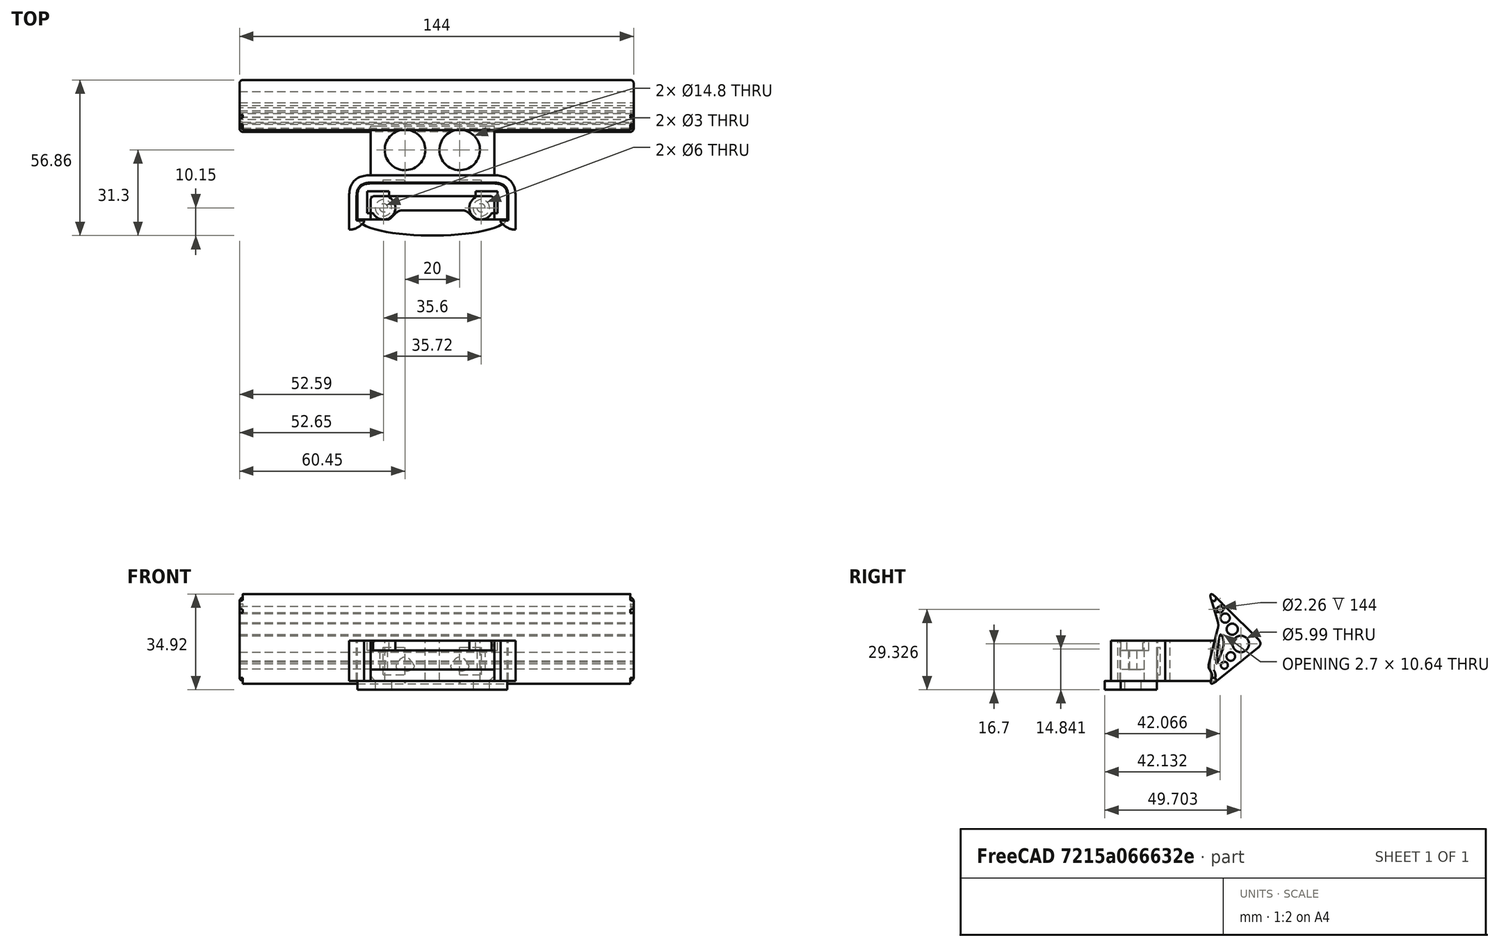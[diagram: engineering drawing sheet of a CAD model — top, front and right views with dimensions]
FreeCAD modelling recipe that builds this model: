
FCSTD DOCUMENT  (FreeCAD 0.19R0.19.2)
Label: 038
License: All rights reserved
LicenseURL: http://en.wikipedia.org/wiki/All_rights_reserved
objects: Sketcher::SketchObject×6, Part::Extrusion×6, Part::Cylinder×4, Part::Box×3, Part::Fillet×3, Part::MultiFuse×2, Part::Cut×2
note: 26 computed .brp shape members not serialized (recipe doc carries the construction recipe); baked Part::Feature solids carry a one-line shape summary decoded from their .brp

FEATURE [Sketcher::SketchObject] Sketch  label="attatchmentPiece"
  FullyConstrained = true
  sketch-geometry (20):
    g0: Circle CenterX=16.25 CenterY=0 CenterZ=0 NormalX=0 NormalY=0 NormalZ=1 AngleXU=0 Radius=1.5
    g1: LineSegment StartX=21.05 StartY=0 StartZ=0 EndX=21.05 EndY=-1 EndZ=0
    g2: LineSegment StartX=21.05 StartY=-1 StartZ=0 EndX=21.05 EndY=-4.3 EndZ=0
    g3: LineSegment StartX=-24.15 StartY=4.3 StartZ=0 EndX=21.05 EndY=4.3 EndZ=0
    g4: LineSegment StartX=21.05 StartY=0 StartZ=0 EndX=21.05 EndY=4.3 EndZ=0
    g5-g8: Circle x4 (B-spline internal-alignment scaffolding for g9; pole/knot coordinates omitted)
    g9: BSplineCurve PolesCount=4 KnotsCount=2 Degree=3 IsPeriodic=0
    g10: GeomPoint X=10.05 Y=-1 Z=0
    g11: GeomPoint X=14.55 Y=-4.3 Z=0
    g12: LineSegment StartX=10.05 StartY=-1 StartZ=0 EndX=-10.05 EndY=-1 EndZ=0
    g13: LineSegment StartX=14.55 StartY=-4.3 StartZ=0 EndX=21.05 EndY=-4.3 EndZ=0
    g14: LineSegment StartX=-24.15 StartY=4.3 StartZ=0 EndX=-24.15 EndY=-4.3 EndZ=0
    g15: LineSegment StartX=-13.15 StartY=-1 StartZ=0 EndX=-10.05 EndY=-1 EndZ=0
    g16: LineSegment StartX=-24.15 StartY=-4.3 StartZ=0 EndX=-19.35 EndY=-4.3 EndZ=0
    g17: Circle CenterX=-19.35 CenterY=0 CenterZ=0 NormalX=0 NormalY=0 NormalZ=1 AngleXU=0 Radius=1.5
    g18: LineSegment StartX=-19.35 StartY=-4.3 StartZ=0 EndX=-17.65 EndY=-4.3 EndZ=0
    g19: BSplineCurve PolesCount=4 KnotsCount=2 Degree=3 IsPeriodic=0
  constraints (41):
    c: Block(g0)
    c: Vertical(g1)
    c: Coincident(g2,g1)
    c: Vertical(g2)
    c: Block(g1)
    c: Horizontal(g3)
    c: Vertical(g4)
    c: Coincident(g4,g3)
    c: Block(g3)
    c: Block(g4)
    c: Weight(g5) = 1
    c: Equal(g5,g6)
    c: Equal(g5,g7)
    c: Equal(g5,g8)
    c: InternalAlignment(g5-g8 -> g9) x4
    c: InternalAlignment(g10,g9)
    c: InternalAlignment(g11,g9)
    c: Block(g9)
    c: Coincident(g12,g9)
    c: Horizontal(g12)
    c: Coincident(g13,g9)
    c: Coincident(g13,g2)
    c: Horizontal(g13)
    c: Distance(g3) = 45.2
    c: Coincident(g14,g3)
    c: Vertical(g14)
    c: Horizontal(g15)
    c: Distance(g15) = 3.1
    c: Block(g17)
    c: Horizontal(g16)
    c: Block(g19)
    c: Coincident(g18,g16)
    c: Coincident(g18,g19)
    c: Horizontal(g18)
    c: Block(g18)
    c: Coincident(g19,g15)
    c: Block(g16)
    c: Block(g12)
    c: Block(g14)
    c: Distance(g16) = 4.8
    c: Distance(g18) = 1.7
FEATURE [Part::Extrusion] Extrude  label="attatchmentPiece001"
  Base = -> Sketch
  Dir = (0,0,1)
  DirMode = 2
  FaceMakerClass = Part::FaceMakerBullseye
  LengthFwd = 7
  LengthRev = 0
  Solid = true
  Symmetric = false
FEATURE [Sketcher::SketchObject] Sketch001  label="attatchmentPieceSurround"
  FullyConstrained = true
  sketch-geometry (18):
    g0: LineSegment StartX=25.85 StartY=-4.3 StartZ=0 EndX=21.05 EndY=-4.3 EndZ=0
    g1: LineSegment StartX=25.85 StartY=-4.3 StartZ=0 EndX=25.85 EndY=4.3 EndZ=0
    g2: LineSegment StartX=-21.05 StartY=8.9 StartZ=0 EndX=21.05 EndY=8.9 EndZ=0
    g3: Circle CenterX=21.05 CenterY=8.9 CenterZ=0 NormalX=0 NormalY=0 NormalZ=1 AngleXU=0 Radius=1
    g4: Circle CenterX=25.85 CenterY=8.9 CenterZ=0 NormalX=0 NormalY=0 NormalZ=1 AngleXU=0 Radius=1
    g5: Circle CenterX=25.85 CenterY=4.3 CenterZ=0 NormalX=0 NormalY=0 NormalZ=1 AngleXU=0 Radius=1
    g6: BSplineCurve PolesCount=3 KnotsCount=2 Degree=2 IsPeriodic=0
    g7: GeomPoint X=21.05 Y=8.9 Z=0
    g8: GeomPoint X=25.85 Y=4.3 Z=0
    g9: ArcOfCircle CenterX=19.45 CenterY=2.7 CenterZ=0 NormalX=0 NormalY=0 NormalZ=1 AngleXU=0 Radius=1.6 StartAngle=0 EndAngle=1.5708
    g10: LineSegment StartX=21.05 StartY=2.7 StartZ=0 EndX=21.05 EndY=-4.3 EndZ=0
    g11: BSplineCurve PolesCount=3 KnotsCount=2 Degree=2 IsPeriodic=0
    g12: LineSegment StartX=-28.95 StartY=-4.3 StartZ=0 EndX=-28.95 EndY=4.3 EndZ=0
    g13: LineSegment StartX=-24.15 StartY=-4.3 StartZ=0 EndX=-28.95 EndY=-4.3 EndZ=0
    g14: LineSegment StartX=-24.15 StartY=2.7 StartZ=0 EndX=-24.15 EndY=-4.3 EndZ=0
    g15: ArcOfCircle CenterX=-22.55 CenterY=2.7 CenterZ=0 NormalX=0 NormalY=0 NormalZ=1 AngleXU=0 Radius=1.6 StartAngle=1.5708 EndAngle=3.14159
    g16: LineSegment StartX=-24.15 StartY=8.9 StartZ=0 EndX=-21.05 EndY=8.9 EndZ=0
    g17: LineSegment StartX=-22.55 StartY=4.3 StartZ=0 EndX=19.45 EndY=4.3 EndZ=0
  constraints (38):
    c: Horizontal(g0)
    c: Vertical(g1)
    c: Coincident(g1,g0)
    c: Horizontal(g2)
    c: Distance(g2) = 42.1
    c: Block(g2)
    c: Coincident(g6,g2)
    c: Weight(g3) = 1
    c: Equal(g3,g4)
    c: Equal(g3,g5)
    c: Coincident(g6,g1)
    c: InternalAlignment(g3,g6)
    c: InternalAlignment(g4,g6)
    c: InternalAlignment(g5,g6)
    c: InternalAlignment(g7,g6)
    c: InternalAlignment(g8,g6)
    c: Block(g0)
    c: Block(g6)
    c: Block(g9)
    c: Coincident(g10,g9)
    c: Coincident(g10,g0)
    c: Vertical(g10)
    c: Horizontal(g13)
    c: Coincident(g12,g13)
    c: Vertical(g12)
    c: Coincident(g11,g12)
    c: Block(g12)
    c: Block(g11)
    c: Block(g15)
    c: Coincident(g14,g15)
    c: Coincident(g14,g13)
    c: Vertical(g14)
    c: Coincident(g16,g11)
    c: Coincident(g16,g2)
    c: Horizontal(g16)
    c: Coincident(g17,g15)
    c: Coincident(g17,g9)
    c: Horizontal(g17)
FEATURE [Part::Extrusion] Extrude001  label="attatchmentPieceSurround001"
  Base = -> Sketch001
  Dir = (0,0,1)
  DirMode = 2
  FaceMakerClass = Part::FaceMakerBullseye
  LengthFwd = 14.7
  LengthRev = 0
  Placement = pos=(0,0,-4.1) rot=(0,0,1;0rad)
  Solid = true
  Symmetric = false
FEATURE [Sketcher::SketchObject] Sketch002  label="attatchmentPieceEndScrewHoleCaps"
  FullyConstrained = true
  sketch-geometry (10):
    g0: ArcOfCircle CenterX=16.25 CenterY=0 CenterZ=0 NormalX=0 NormalY=0 NormalZ=1 AngleXU=0 Radius=4.3 StartAngle=2.05456 EndAngle=5.79942
    g1: LineSegment StartX=14.25 StartY=3.80657 StartZ=0 EndX=14.25 EndY=6 EndZ=0
    g2: LineSegment StartX=20.0566 StartY=-2 StartZ=0 EndX=22.25 EndY=-2 EndZ=0
    g3: LineSegment StartX=22.25 StartY=-2 StartZ=0 EndX=22.25 EndY=6 EndZ=0
    g4: LineSegment StartX=14.25 StartY=6 StartZ=0 EndX=22.25 EndY=6 EndZ=0
    g5: LineSegment StartX=-25.35 StartY=-2 StartZ=0 EndX=-25.35 EndY=6 EndZ=0
    g6: LineSegment StartX=-25.35 StartY=-2 StartZ=0 EndX=-23.1566 EndY=-2 EndZ=0
    g7: LineSegment StartX=-17.35 StartY=6 StartZ=0 EndX=-25.35 EndY=6 EndZ=0
    g8: LineSegment StartX=-17.35 StartY=3.80657 StartZ=0 EndX=-17.35 EndY=6 EndZ=0
    g9: ArcOfCircle CenterX=-19.35 CenterY=0 CenterZ=0 NormalX=0 NormalY=0 NormalZ=1 AngleXU=0 Radius=4.3 StartAngle=3.62536 EndAngle=7.37022
  constraints (25):
    c: Block(g0)
    c: Vertical(g1)
    c: Horizontal(g2)
    c: Coincident(g3,g2)
    c: Vertical(g3)
    c: Coincident(g4,g1)
    c: Horizontal(g4)
    c: Coincident(g3,g4)
    c: Block(g4)
    c: Block(g3)
    c: Coincident(g0,g1)
    c: Coincident(g0,g2)
    c: Block(g1)
    c: Block(g9)
    c: Horizontal(g6)
    c: Vertical(g8)
    c: Coincident(g7,g8)
    c: Horizontal(g7)
    c: Coincident(g5,g6)
    c: Vertical(g5)
    c: Coincident(g5,g7)
    c: Block(g7)
    c: Block(g5)
    c: Coincident(g9,g6)
    c: Coincident(g9,g8)
FEATURE [Part::Extrusion] Extrude002  label="attatchmentPieceEndScrewHoleCaps001"
  Base = -> Sketch002
  Dir = (0,0,1)
  DirMode = 2
  FaceMakerClass = Part::FaceMakerBullseye
  LengthFwd = 3.6
  LengthRev = 0
  Placement = pos=(0,0,7) rot=(0,0,1;0rad)
  Solid = true
  Symmetric = false
FEATURE [Sketcher::SketchObject] Sketch003  label="mainBumpperPieceAttatchment"
  FullyConstrained = true
  sketch-geometry (42):
    g0: Circle CenterX=28.85 CenterY=4.3 CenterZ=0 NormalX=0 NormalY=0 NormalZ=1 AngleXU=0 Radius=1
    g1: Circle CenterX=28.85 CenterY=11.9 CenterZ=0 NormalX=0 NormalY=0 NormalZ=1 AngleXU=0 Radius=1
    g2: Circle CenterX=21.05 CenterY=11.9 CenterZ=0 NormalX=0 NormalY=0 NormalZ=1 AngleXU=0 Radius=1
    g3: BSplineCurve PolesCount=3 KnotsCount=2 Degree=2 IsPeriodic=0
    g4: GeomPoint X=28.85 Y=4.3 Z=0
    g5: GeomPoint X=21.05 Y=11.9 Z=0
    g6: LineSegment StartX=-21.05 StartY=11.9 StartZ=0 EndX=21.05 EndY=11.9 EndZ=0
    g7: LineSegment StartX=28.85 StartY=4.3 StartZ=0 EndX=28.85 EndY=-4.3 EndZ=0
    g8: Circle CenterX=21.05 CenterY=9.2 CenterZ=0 NormalX=0 NormalY=0 NormalZ=1 AngleXU=0 Radius=1
    g9: Circle CenterX=26.15 CenterY=9.2 CenterZ=0 NormalX=0 NormalY=0 NormalZ=1 AngleXU=0 Radius=1
    g10: Circle CenterX=26.15 CenterY=4.3 CenterZ=0 NormalX=0 NormalY=0 NormalZ=1 AngleXU=0 Radius=1
    g11: BSplineCurve PolesCount=3 KnotsCount=2 Degree=2 IsPeriodic=0
    g12: GeomPoint X=21.05 Y=9.2 Z=0
    g13: GeomPoint X=26.15 Y=4.3 Z=0
    g14: LineSegment StartX=-21.05 StartY=9.2 StartZ=0 EndX=21.05 EndY=9.2 EndZ=0
    g15: LineSegment StartX=26.15 StartY=-4.3 StartZ=0 EndX=26.15 EndY=4.3 EndZ=0
    g16: LineSegment StartX=26.15 StartY=-4.3 StartZ=0 EndX=26.15 EndY=-4.6 EndZ=0
    g17: LineSegment StartX=23.45 StartY=-4.6 StartZ=0 EndX=26.15 EndY=-4.6 EndZ=0
    g18: LineSegment StartX=28.85 StartY=-4.3 StartZ=0 EndX=28.85 EndY=-7.9 EndZ=0
    g19: LineSegment StartX=23.45 StartY=-4.6 StartZ=0 EndX=23.45 EndY=-5.3 EndZ=0
    g20: Circle CenterX=28.85 CenterY=-7.9 CenterZ=0 NormalX=0 NormalY=0 NormalZ=1 AngleXU=0 Radius=1
    g21: Circle CenterX=26.15 CenterY=-8.2 CenterZ=0 NormalX=0 NormalY=0 NormalZ=1 AngleXU=0 Radius=1
    g22: Circle CenterX=23.45 CenterY=-5.3 CenterZ=0 NormalX=0 NormalY=0 NormalZ=1 AngleXU=0 Radius=1
    g23: BSplineCurve PolesCount=3 KnotsCount=2 Degree=2 IsPeriodic=0
    g24: GeomPoint X=28.85 Y=-7.9 Z=0
    g25: GeomPoint X=23.45 Y=-5.3 Z=0
    g26: LineSegment StartX=-21.05 StartY=9.2 StartZ=0 EndX=-24.15 EndY=9.2 EndZ=0
    g27: BSplineCurve PolesCount=3 KnotsCount=2 Degree=2 IsPeriodic=0
    g28: LineSegment StartX=-29.25 StartY=-4.3 StartZ=0 EndX=-29.25 EndY=-4.6 EndZ=0
    g29: LineSegment StartX=-29.25 StartY=-4.6 StartZ=0 EndX=-26.55 EndY=-4.6 EndZ=0
    g30: LineSegment StartX=-31.95 StartY=-4.3 StartZ=0 EndX=-31.95 EndY=-7.9 EndZ=0
    g31: LineSegment StartX=-26.55 StartY=-4.6 StartZ=0 EndX=-26.55 EndY=-5.3 EndZ=0
    g32: Circle CenterX=-31.95 CenterY=-7.9 CenterZ=0 NormalX=0 NormalY=0 NormalZ=1 AngleXU=0 Radius=1
    g33: Circle CenterX=-29.25 CenterY=-8.2 CenterZ=0 NormalX=0 NormalY=0 NormalZ=1 AngleXU=0 Radius=1
    g34: Circle CenterX=-26.55 CenterY=-5.3 CenterZ=0 NormalX=0 NormalY=0 NormalZ=1 AngleXU=0 Radius=1
    g35: BSplineCurve PolesCount=3 KnotsCount=2 Degree=2 IsPeriodic=0
    g36: GeomPoint X=-31.95 Y=-7.9 Z=0
    g37: GeomPoint X=-26.55 Y=-5.3 Z=0
    g38: LineSegment StartX=-31.95 StartY=4.3 StartZ=0 EndX=-31.95 EndY=-4.3 EndZ=0
    g39: LineSegment StartX=-29.25 StartY=-4.3 StartZ=0 EndX=-29.25 EndY=4.3 EndZ=0
    g40: BSplineCurve PolesCount=3 KnotsCount=2 Degree=2 IsPeriodic=0
    g41: LineSegment StartX=-21.05 StartY=11.9 StartZ=0 EndX=-24.15 EndY=11.9 EndZ=0
  constraints (78):
    c: Weight(g0) = 1
    c: Equal(g0,g1)
    c: Equal(g0,g2)
    c: InternalAlignment(g0,g3)
    c: InternalAlignment(g1,g3)
    c: InternalAlignment(g2,g3)
    c: InternalAlignment(g4,g3)
    c: InternalAlignment(g5,g3)
    c: Block(g3)
    c: Horizontal(g6)
    c: Vertical(g7)
    c: Block(g7)
    c: Block(g6)
    c: Weight(g8) = 1
    c: Equal(g8,g9)
    c: Equal(g8,g10)
    c: InternalAlignment(g8,g11)
    c: InternalAlignment(g9,g11)
    c: InternalAlignment(g10,g11)
    c: InternalAlignment(g12,g11)
    c: InternalAlignment(g13,g11)
    c: Horizontal(g14)
    c: Vertical(g15)
    c: Block(g11)
    c: Block(g15)
    c: Block(g14)
    c: Coincident(g16,g15)
    c: Vertical(g16)
    c: Distance(g16) = 0.3
    c: Horizontal(g17)
    c: Coincident(g17,g16)
    c: Coincident(g18,g7)
    c: Vertical(g18)
    c: Distance(g18) = 3.6
    c: Vertical(g19)
    c: Coincident(g19,g17)
    c: Coincident(g23,g18)
    c: Weight(g20) = 1
    c: Equal(g20,g21)
    c: Equal(g20,g22)
    c: Coincident(g23,g19)
    c: InternalAlignment(g20,g23)
    c: InternalAlignment(g21,g23)
    c: InternalAlignment(g22,g23)
    c: InternalAlignment(g24,g23)
    c: InternalAlignment(g25,g23)
    c: Block(g23)
    c: Horizontal(g26)
    c: Distance(g26) = 3.1
    c: Block(g27)
    c: Vertical(g38)
    c: Block(g38)
    c: Vertical(g39)
    c: Block(g40)
    c: Block(g39)
    c: Vertical(g28)
    c: Coincident(g28,g39)
    c: Coincident(g29,g28)
    c: Horizontal(g29)
    c: Vertical(g30)
    c: Coincident(g30,g38)
    c: Coincident(g31,g29)
    c: Vertical(g31)
    c: Coincident(g35,g30)
    c: Equal(g32,g33)
    c: Equal(g32,g34)
    c: Coincident(g35,g31)
    c: InternalAlignment(g32,g35)
    c: InternalAlignment(g33,g35)
    c: InternalAlignment(g34,g35)
    c: InternalAlignment(g36,g35)
    c: InternalAlignment(g37,g35)
    c: Block(g35)
    c: Coincident(g40,g26)
    c: Block(g29)
    c: Horizontal(g41)
    c: Equal(g26,g41) = 3.1
    c: Coincident(g41,g6)
FEATURE [Part::Box] Box  label="bumpperExtension"
  AttacherType = Attacher::AttachEngine3D
  Height = 14.7
  Length = 45.2
  Placement = pos=(-24.15,11.9,-4.1) rot=(0,0,1;0rad)
  Width = 18
FEATURE [Sketcher::SketchObject] Sketch004  label="bumpperMain"
  FullyConstrained = true
  Placement = pos=(0,0,0) rot=(0.57735,0.57735,0.57735;2.0944rad)
  sketch-geometry (62):
    g0: Circle CenterX=-3.12329 CenterY=2.49901 CenterZ=0 NormalX=0 NormalY=0 NormalZ=1 AngleXU=0 Radius=1
    g1: Circle CenterX=0 CenterY=0 CenterZ=0 NormalX=0 NormalY=0 NormalZ=1 AngleXU=0 Radius=1
    g2: Circle CenterX=-1.35243 CenterY=3.60648 CenterZ=0 NormalX=0 NormalY=0 NormalZ=1 AngleXU=0 Radius=1
    g3: BSplineCurve PolesCount=3 KnotsCount=2 Degree=2 IsPeriodic=0
    g4: GeomPoint X=-3.12329 Y=2.49901 Z=0
    g5: GeomPoint X=-1.35243 Y=3.60648 Z=0
    g6: Circle CenterX=-2.83953 CenterY=33.0261 CenterZ=0 NormalX=0 NormalY=0 NormalZ=1 AngleXU=0 Radius=1
    g7: Circle CenterX=0 CenterY=35.8434 CenterZ=0 NormalX=0 NormalY=0 NormalZ=1 AngleXU=0 Radius=1
    g8: Circle CenterX=-1.15771 CenterY=32.0146 CenterZ=0 NormalX=0 NormalY=0 NormalZ=1 AngleXU=0 Radius=1
    g9: BSplineCurve PolesCount=3 KnotsCount=2 Degree=2 IsPeriodic=0
    g10: GeomPoint X=-2.83953 Y=33.0261 Z=0
    g11: GeomPoint X=-1.15771 Y=32.0146 Z=0
    g12: Circle CenterX=-18.2963 CenterY=17.6904 CenterZ=0 NormalX=0 NormalY=0 NormalZ=1 AngleXU=0 Radius=1
    g13: Circle CenterX=-20 CenterY=16 CenterZ=0 NormalX=0 NormalY=0 NormalZ=1 AngleXU=0 Radius=1
    g14: Circle CenterX=-18.1259 CenterY=14.5008 CenterZ=0 NormalX=0 NormalY=0 NormalZ=1 AngleXU=0 Radius=1
    g15: BSplineCurve PolesCount=3 KnotsCount=2 Degree=2 IsPeriodic=0
    g16: GeomPoint X=-18.2963 Y=17.6904 Z=0
    g17: GeomPoint X=-18.1259 Y=14.5008 Z=0
    g18: LineSegment StartX=-18.2963 StartY=17.6904 StartZ=0 EndX=-2.83953 EndY=33.0261 EndZ=0
    g19: LineSegment StartX=-18.1259 StartY=14.5008 StartZ=0 EndX=-3.12329 EndY=2.49901 EndZ=0
    g20: Circle CenterX=-11.9527 CenterY=16 CenterZ=0 NormalX=0 NormalY=0 NormalZ=1 AngleXU=0 Radius=2.99582
    g21: Circle CenterX=-8.803 CenterY=21.3731 CenterZ=0 NormalX=0 NormalY=0 NormalZ=1 AngleXU=0 Radius=2.03939
    g22: Circle CenterX=-6.23123 CenterY=25.4475 CenterZ=0 NormalX=0 NormalY=0 NormalZ=1 AngleXU=0 Radius=1.69309
    g23: Circle CenterX=-4.38186 CenterY=28.6261 CenterZ=0 NormalX=0 NormalY=0 NormalZ=1 AngleXU=0 Radius=1.13029
    g24: Circle CenterX=-8.28033 CenterY=11.4296 CenterZ=0 NormalX=0 NormalY=0 NormalZ=1 AngleXU=0 Radius=1.57213
    g25: Circle CenterX=-5.93972 CenterY=8.22213 CenterZ=0 NormalX=0 NormalY=0 NormalZ=1 AngleXU=0 Radius=1.28743
    g26: Circle CenterX=-3.47023 CenterY=24.3665 CenterZ=0 NormalX=0 NormalY=0 NormalZ=1 AngleXU=0 Radius=1
    g27: Circle CenterX=-3.90437 CenterY=22.9307 CenterZ=0 NormalX=0 NormalY=0 NormalZ=1 AngleXU=0 Radius=1
    g28: Circle CenterX=-3.53772 CenterY=21.4762 CenterZ=0 NormalX=0 NormalY=0 NormalZ=1 AngleXU=0 Radius=1
    g29: BSplineCurve PolesCount=3 KnotsCount=2 Degree=2 IsPeriodic=0
    g30: GeomPoint X=-3.47023 Y=24.3665 Z=0
    g31: GeomPoint X=-3.53772 Y=21.4762 Z=0
    g32: LineSegment StartX=-1.15771 StartY=32.0146 StartZ=0 EndX=-3.47023 EndY=24.3665 EndZ=0
    g33: Circle CenterX=-5.41867 CenterY=17.9226 CenterZ=0 NormalX=0 NormalY=0 NormalZ=1 AngleXU=0 Radius=1
    g34: Circle CenterX=-6 CenterY=16 CenterZ=0 NormalX=0 NormalY=0 NormalZ=1 AngleXU=0 Radius=1
    g35: Circle CenterX=-5.22753 CenterY=13.9401 CenterZ=0 NormalX=0 NormalY=0 NormalZ=1 AngleXU=0 Radius=1
    g36: BSplineCurve PolesCount=3 KnotsCount=2 Degree=2 IsPeriodic=0
    g37: GeomPoint X=-5.41867 Y=17.9226 Z=0
    g38: GeomPoint X=-5.22753 Y=13.9401 Z=0
    g39: Circle CenterX=-3.98946 CenterY=10.6386 CenterZ=0 NormalX=0 NormalY=0 NormalZ=1 AngleXU=0 Radius=1
    g40: Circle CenterX=-2.58497 CenterY=6.89324 CenterZ=0 NormalX=0 NormalY=0 NormalZ=1 AngleXU=0 Radius=1
    g41: Circle CenterX=-3.11001 CenterY=10.8586 CenterZ=0 NormalX=0 NormalY=0 NormalZ=1 AngleXU=0 Radius=1
    g42: BSplineCurve PolesCount=3 KnotsCount=2 Degree=2 IsPeriodic=0
    g43: GeomPoint X=-3.98946 Y=10.6386 Z=0
    g44: GeomPoint X=-3.11001 Y=10.8586 Z=0
    g45: Circle CenterX=-1.35243 CenterY=3.60648 CenterZ=0 NormalX=0 NormalY=0 NormalZ=1 AngleXU=0 Radius=1
    g46: Circle CenterX=-1.76142 CenterY=4.69712 CenterZ=0 NormalX=0 NormalY=0 NormalZ=1 AngleXU=0 Radius=1
    g47: Circle CenterX=-1.05937 CenterY=5.79125 CenterZ=0 NormalX=0 NormalY=0 NormalZ=1 AngleXU=0 Radius=1
    g48: BSplineCurve PolesCount=3 KnotsCount=2 Degree=2 IsPeriodic=0
    g49: GeomPoint X=-1.35243 Y=3.60648 Z=0
    g50: GeomPoint X=-1.05937 Y=5.79125 Z=0
    g51: Circle CenterX=-0.519336 CenterY=6.6329 CenterZ=0 NormalX=0 NormalY=0 NormalZ=1 AngleXU=0 Radius=1
    g52: Circle CenterX=0 CenterY=7.44228 CenterZ=0 NormalX=0 NormalY=0 NormalZ=1 AngleXU=0 Radius=1
    g53: Circle CenterX=-0.244436 CenterY=8.41194 CenterZ=0 NormalX=0 NormalY=0 NormalZ=1 AngleXU=0 Radius=1
    g54: BSplineCurve PolesCount=3 KnotsCount=2 Degree=2 IsPeriodic=0
    g55: GeomPoint X=-0.519336 Y=6.6329 Z=0
    g56: GeomPoint X=-0.244436 Y=8.41194 Z=0
    g57: LineSegment StartX=-3.53772 StartY=21.4762 StartZ=0 EndX=-0.244436 EndY=8.41194 EndZ=0
    g58: LineSegment StartX=-5.22753 StartY=13.9401 StartZ=0 EndX=-3.98946 EndY=10.6386 EndZ=0
    g59: LineSegment StartX=-1.05937 StartY=5.79125 StartZ=0 EndX=-0.519336 EndY=6.6329 EndZ=0
    g60: BSplineCurve PolesCount=3 KnotsCount=2 Degree=2 IsPeriodic=0
    g61: LineSegment StartX=-4.0304 StartY=17.8099 StartZ=0 EndX=-3.11001 EndY=10.8586 EndZ=0
  constraints (96):
    c: Weight(g0) = 1
    c: Equal(g0,g1)
    c: Equal(g0,g2)
    c: InternalAlignment(g0,g3)
    c: InternalAlignment(g1,g3)
    c: InternalAlignment(g2,g3)
    c: InternalAlignment(g4,g3)
    c: InternalAlignment(g5,g3)
    c: Block(g3)
    c: Weight(g6) = 1
    c: Equal(g6,g7)
    c: Equal(g6,g8)
    c: InternalAlignment(g6,g9)
    c: InternalAlignment(g7,g9)
    c: InternalAlignment(g8,g9)
    c: InternalAlignment(g10,g9)
    c: InternalAlignment(g11,g9)
    c: Block(g9)
    c: Weight(g12) = 1
    c: Equal(g12,g13)
    c: Equal(g12,g14)
    c: InternalAlignment(g12,g15)
    c: InternalAlignment(g13,g15)
    c: InternalAlignment(g14,g15)
    c: InternalAlignment(g16,g15)
    c: InternalAlignment(g17,g15)
    c: Block(g15)
    c: Coincident(g18,g15)
    c: Coincident(g18,g9)
    c: Coincident(g19,g15)
    c: Coincident(g19,g3)
    c: Block(g25)
    c: Block(g24)
    c: Block(g20)
    c: Block(g21)
    c: Block(g22)
    c: Block(g23)
    c: Weight(g26) = 1
    c: Equal(g26,g27)
    c: Equal(g26,g28)
    c: InternalAlignment(g26,g29)
    c: InternalAlignment(g27,g29)
    c: InternalAlignment(g28,g29)
    c: InternalAlignment(g30,g29)
    c: InternalAlignment(g31,g29)
    c: Block(g29)
    c: Coincident(g32,g9)
    c: Coincident(g32,g29)
    c: Weight(g33) = 1
    c: Equal(g33,g34)
    c: Equal(g33,g35)
    c: InternalAlignment(g33,g36)
    c: InternalAlignment(g34,g36)
    c: InternalAlignment(g35,g36)
    c: InternalAlignment(g37,g36)
    c: InternalAlignment(g38,g36)
    c: Block(g36)
    c: Weight(g39) = 1
    c: Equal(g39,g40)
    c: Equal(g39,g41)
    c: InternalAlignment(g39,g42)
    c: InternalAlignment(g40,g42)
    c: InternalAlignment(g41,g42)
    c: InternalAlignment(g43,g42)
    c: InternalAlignment(g44,g42)
    c: Block(g42)
    c: Coincident(g48,g3)
    c: Weight(g45) = 1
    c: Equal(g45,g46)
    c: Equal(g45,g47)
    c: InternalAlignment(g45,g48)
    c: InternalAlignment(g46,g48)
    c: InternalAlignment(g47,g48)
    c: InternalAlignment(g49,g48)
    c: InternalAlignment(g50,g48)
    c: Block(g48)
    c: Weight(g51) = 1
    c: Equal(g51,g52)
    c: Equal(g51,g53)
    c: InternalAlignment(g51,g54)
    c: InternalAlignment(g52,g54)
    c: InternalAlignment(g53,g54)
    c: InternalAlignment(g55,g54)
    c: InternalAlignment(g56,g54)
    c: Block(g54)
    c: Coincident(g57,g29)
    c: Coincident(g57,g54)
    c: Block(g57)
    c: Coincident(g58,g36)
    c: Coincident(g58,g42)
    c: Coincident(g59,g48)
    c: Coincident(g59,g54)
    c: Block(g60)
    c: Coincident(g60,g36)
    c: Coincident(g61,g60)
    c: Coincident(g61,g42)
FEATURE [Part::Extrusion] Extrude004  label="bumpperMain001"
  Base = -> Sketch004
  Dir = (1,0,0)
  DirMode = 2
  FaceMakerClass = Part::FaceMakerBullseye
  LengthFwd = 144
  LengthRev = 0
  Placement = pos=(72,27.6,-6.6) rot=(0,0,1;3.14159rad)
  Solid = true
  Symmetric = false
FEATURE [Sketcher::SketchObject] Sketch005  label="attatchmentPieceBottom"
  FullyConstrained = true
  sketch-geometry (20):
    g0: LineSegment StartX=25.85 StartY=-4.3 StartZ=0 EndX=25.85 EndY=4.3 EndZ=0
    g1: LineSegment StartX=-21.05 StartY=8.9 StartZ=0 EndX=21.05 EndY=8.9 EndZ=0
    g2: Circle CenterX=21.05 CenterY=8.9 CenterZ=0 NormalX=0 NormalY=0 NormalZ=1 AngleXU=0 Radius=1
    g3: Circle CenterX=25.85 CenterY=8.9 CenterZ=0 NormalX=0 NormalY=0 NormalZ=1 AngleXU=0 Radius=1
    g4: Circle CenterX=25.85 CenterY=4.3 CenterZ=0 NormalX=0 NormalY=0 NormalZ=1 AngleXU=0 Radius=1
    g5: BSplineCurve PolesCount=3 KnotsCount=2 Degree=2 IsPeriodic=0
    g6: GeomPoint X=21.05 Y=8.9 Z=0
    g7: GeomPoint X=25.85 Y=4.3 Z=0
    g8: BSplineCurve PolesCount=3 KnotsCount=2 Degree=2 IsPeriodic=0
    g9: LineSegment StartX=-28.95 StartY=-4.3 StartZ=0 EndX=-28.95 EndY=4.3 EndZ=0
    g10: LineSegment StartX=-24.15 StartY=8.9 StartZ=0 EndX=-21.05 EndY=8.9 EndZ=0
    g11: Circle CenterX=-19.41 CenterY=0 CenterZ=0 NormalX=0 NormalY=0 NormalZ=1 AngleXU=0 Radius=3
    g12: Circle CenterX=16.3103 CenterY=0 CenterZ=0 NormalX=0 NormalY=0 NormalZ=1 AngleXU=0 Radius=3
    g13-g16: Circle x4 (B-spline internal-alignment scaffolding for g17; pole/knot coordinates omitted)
    g17: BSplineCurve PolesCount=4 KnotsCount=2 Degree=3 IsPeriodic=0
    g18: GeomPoint X=-28.95 Y=-4.3 Z=0
    g19: GeomPoint X=25.85 Y=-4.3 Z=0
  constraints (36):
    c: Vertical(g0)
    c: Horizontal(g1)
    c: Distance(g1) = 42.1
    c: Block(g1)
    c: Coincident(g5,g1)
    c: Weight(g2) = 1
    c: Equal(g2,g3)
    c: Equal(g2,g4)
    c: Coincident(g5,g0)
    c: InternalAlignment(g2,g5)
    c: InternalAlignment(g3,g5)
    c: InternalAlignment(g4,g5)
    c: InternalAlignment(g6,g5)
    c: InternalAlignment(g7,g5)
    c: Block(g5)
    c: Vertical(g9)
    c: Coincident(g8,g9)
    c: Block(g9)
    c: Block(g8)
    c: Coincident(g10,g8)
    c: Coincident(g10,g1)
    c: Horizontal(g10)
    c: PointOnObject(g12,g-1)
    c: PointOnObject(g11,g-1)
    c: Block(g11)
    c: Block(g12)
    c: Coincident(g17,g9)
    c: Weight(g13) = 1
    c: Equal(g13,g14)
    c: Equal(g13,g15)
    c: Equal(g13,g16)
    c: Coincident(g17,g0)
    c: InternalAlignment(g13-g16 -> g17) x4
    c: InternalAlignment(g18,g17)
    c: InternalAlignment(g19,g17)
    c: Block(g17)
FEATURE [Part::Extrusion] Extrude005  label="attatchmentPieceBottom001"
  Base = -> Sketch005
  Dir = (0,0,1)
  DirMode = 2
  FaceMakerClass = Part::FaceMakerBullseye
  LengthFwd = 3.2
  LengthRev = 0
  Placement = pos=(0,0,-7.3) rot=(0,0,1;0rad)
  Solid = true
  Symmetric = false
FEATURE [Part::Extrusion] Extrude006  label="mainBumpperPieceAttatchment001"
  Base = -> Sketch003
  Dir = (0,0,1)
  DirMode = 2
  FaceMakerClass = Part::FaceMakerBullseye
  LengthFwd = 14.7
  LengthRev = 0
  Placement = pos=(0,0,-4.1) rot=(0,0,1;0rad)
  Solid = true
  Symmetric = false
FEATURE [Part::Cylinder] Cylinder  label="removeFromBumpperExtension"
  Angle = 360
  AttacherType = Attacher::AttachEngine3D
  Height = 20
  Placement = pos=(8.45,21.15,-8) rot=(0,0,1;0rad)
  Radius = 7.4
FEATURE [Part::Cylinder] Cylinder001  label="removeFromBumpperExtension001"
  Angle = 360
  AttacherType = Attacher::AttachEngine3D
  Height = 20
  Placement = pos=(-11.55,21.15,-8) rot=(0,0,1;0rad)
  Radius = 7.4
FEATURE [Part::MultiFuse] Fusion  label="removeFromBumpperExtension002"
  Shapes = -> [Cylinder,Cylinder001]
FEATURE [Part::Cylinder] Cylinder002  label="removeFromBumpperExtension004"
  Angle = 360
  AttacherType = Attacher::AttachEngine3D
  Height = 20
  Placement = pos=(8.45,21.15,-8) rot=(0,0,1;0rad)
  Radius = 7.4
FEATURE [Part::Cylinder] Cylinder003  label="removeFromBumpperExtension005"
  Angle = 360
  AttacherType = Attacher::AttachEngine3D
  Height = 20
  Placement = pos=(-11.55,21.15,-8) rot=(0,0,1;0rad)
  Radius = 7.4
FEATURE [Part::MultiFuse] Fusion001  label="removeFromBumpperMain"
  Shapes = -> [Cylinder002,Cylinder003]
FEATURE [Part::Cut] Cut  label="bumpperExtension001"
  Base = -> Box
  Tool = -> Fusion
FEATURE [Part::Cut] Cut001  label="bumpperMain002"
  Base = -> Extrude004
  Tool = -> Fusion001
FEATURE [Part::Fillet] Fillet  label="bumpperExtension002"
  Base = -> Cut
  Edges = 4 edges r=3: [Edge2,Edge4,Edge9,Edge14]
FEATURE [Part::Fillet] Fillet001
  Base = -> Cut001
  Edges = 11 edges r=1.2: [Edge4,Edge7,Edge10,Edge30,Edge31,Edge32,Edge33,Edge34,Edge35,Edge36,Edge37]
FEATURE [Part::Fillet] Fillet002  label="bumpperMain003"
  Base = -> Fillet001
  Edges = 11 edges r=1.2: [Edge4,Edge9,Edge13,Edge14,Edge15,Edge16,Edge17,Edge18,Edge19,Edge20,Edge21]
FEATURE [Part::Box] Box001  label="Cube"
  AttacherType = Attacher::AttachEngine3D
  Height = 10
  Length = 8
  Placement = pos=(8.45,8.9,-1.8) rot=(0,0,1;0rad)
  Width = 1.3
FEATURE [Part::Box] Box002  label="Cube001"
  AttacherType = Attacher::AttachEngine3D
  Height = 10
  Length = 8
  Placement = pos=(-19.55,8.9,-1.8) rot=(0,0,1;0rad)
  Width = 1.3
